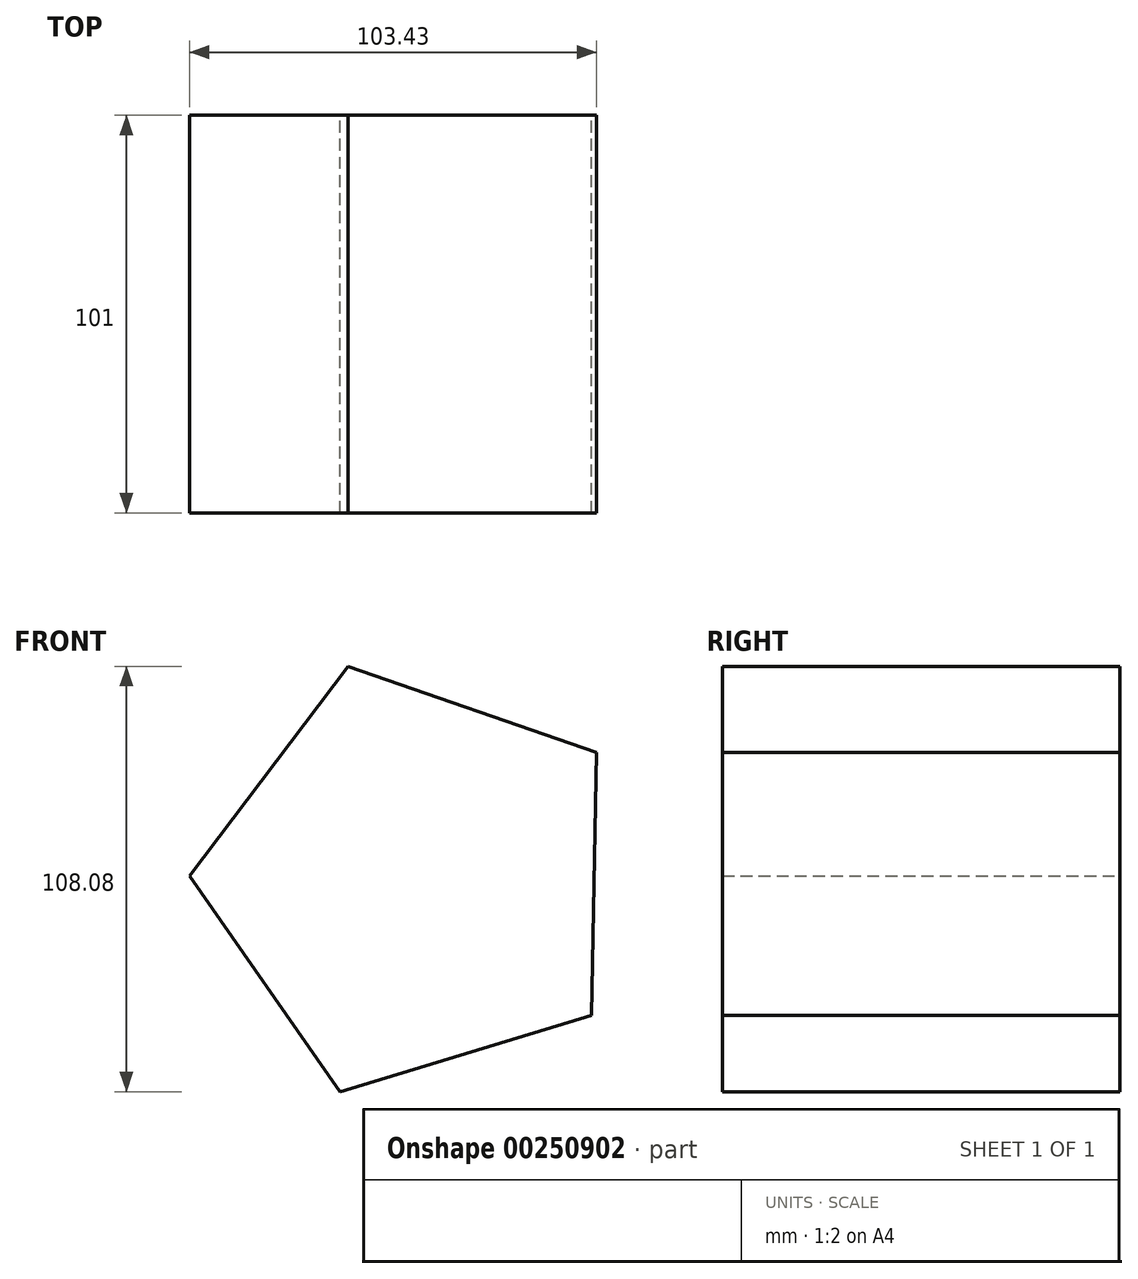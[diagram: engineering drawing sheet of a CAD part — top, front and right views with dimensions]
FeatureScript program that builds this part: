
annotation { "Feature Type Name" : "Feature", "Feature Type Description" : "" }
export const myFeature = defineFeature(function(context is Context, id is Id, definition is map)
    precondition{}
    {
        {
            var Q0;
            Q0=qCreatedBy(makeId("Front.planeOp"),FACE);
            var sketch = newSketch(context, id + "F0", { "sketchPlane" : qUnion([Q0])});
            skCircle(sketch, "E0.cCircle", {"center": v(0, 0) * mm, "radius": 56.83 * mm, "construction": true});
            skLineSegment(sketch, "E0.0", {"start": v(45.33, -34.28) * mm, "end": v(-18.6, -53.7) * mm});
            skLineSegment(sketch, "E0.1", {"start": v(-18.6, -53.7) * mm, "end": v(-56.82, 1.1) * mm});
            skLineSegment(sketch, "E0.2", {"start": v(-56.82, 1.1) * mm, "end": v(-16.52, 54.38) * mm});
            skLineSegment(sketch, "E0.3", {"start": v(-16.52, 54.38) * mm, "end": v(46.61, 32.52) * mm});
            skLineSegment(sketch, "E0.4", {"start": v(46.61, 32.52) * mm, "end": v(45.33, -34.28) * mm});
            skSolve(sketch);
        }
        {
            var Q0;
            Q0=makeQuery(id+"F0.imprint","IMPRINT",FACE,{"disambiguationData":[TD([[makeQuery(id+"F0.imprint","IMPRINT",EDGE,{"derivedFrom":sQuery(id+"F0.wireOp",EDGE,"E0.0")}),-1.0]])]});
            extrude(context, id + "F1", {"entities" : qUnion([Q0]), "endBound" : BoundingType.SYMMETRIC, "depth" : 101 * mm});
        }
    });
